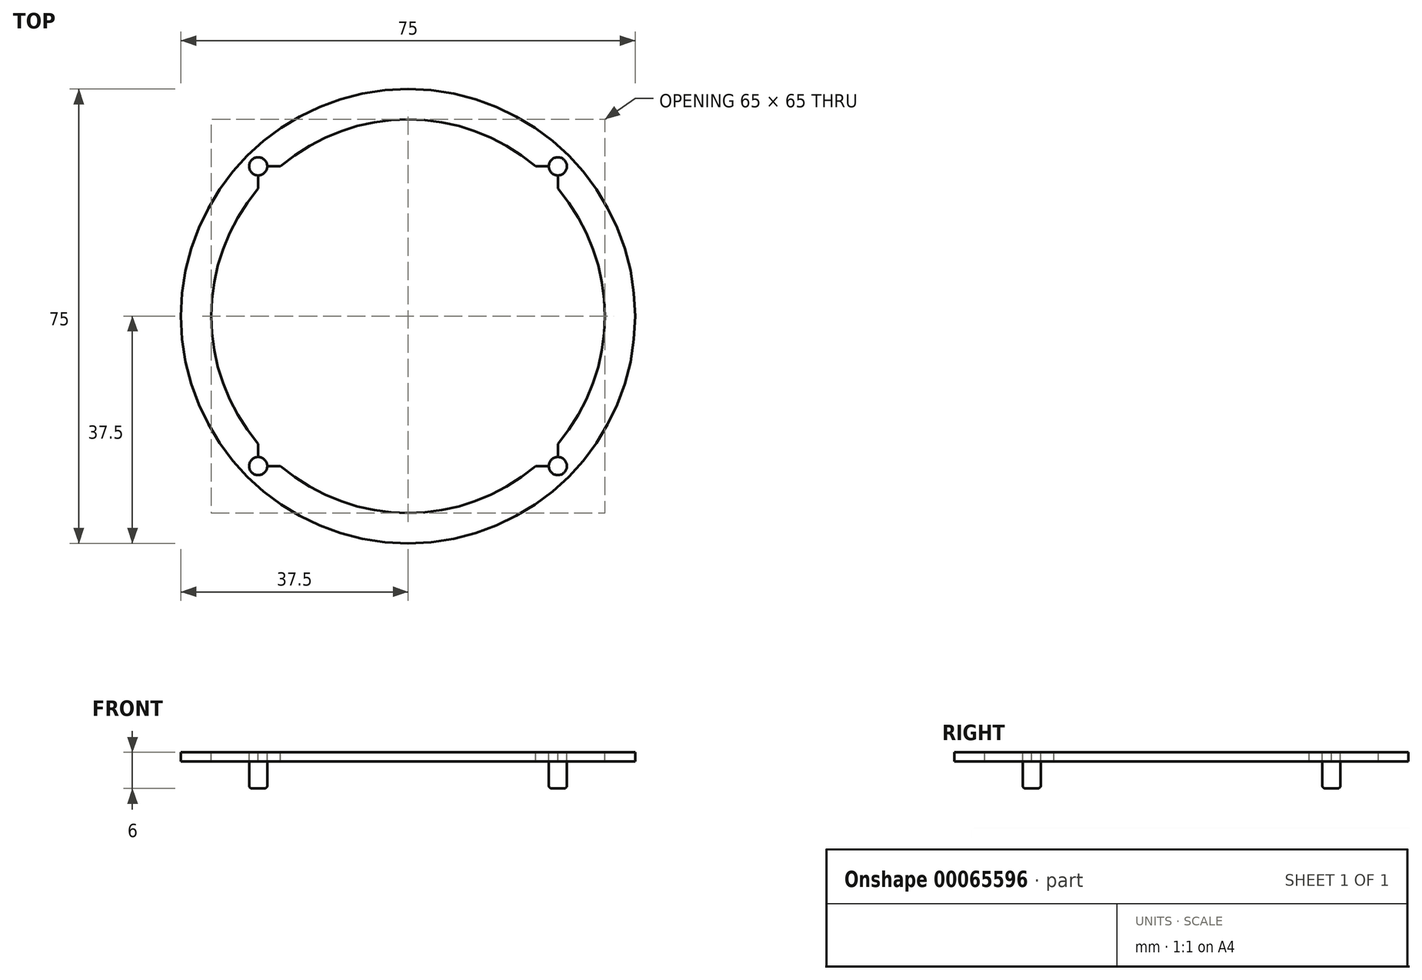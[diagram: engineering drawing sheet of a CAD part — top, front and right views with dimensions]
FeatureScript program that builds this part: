
annotation { "Feature Type Name" : "Feature", "Feature Type Description" : "" }
export const myFeature = defineFeature(function(context is Context, id is Id, definition is map)
    precondition{}
    {
        {
            var Q0;
            Q0=qCreatedBy(makeId("Top.planeOp"),FACE);
            cPlane(context, id + "F0", {"entities" : qUnion([Q0]), "cplaneType" : CPlaneType.OFFSET, "offset" : 1 * mm, "oppositeDirection" : true, "width" : 150 * mm, "height" : 150 * mm});
        }
        {
            var Q0;
            Q0=qCreatedBy(id+"F0.planeOp",FACE);
            var sketch = newSketch(context, id + "F1", { "sketchPlane" : qUnion([Q0])});
            skCircle(sketch, "E0", {"center": v(0, 0) * mm, "radius": 37.5 * mm});
            skCircle(sketch, "E1", {"center": v(0, 0) * mm, "radius": 32.5 * mm});
            skLineSegment(sketch, "E2", {"start": v(0, 0) * mm, "end": v(58.14, 58.14) * mm, "construction": true});
            skLineSegment(sketch, "E3", {"start": v(0, 0) * mm, "end": v(-49.5, 49.5) * mm, "construction": true});
            skLineSegment(sketch, "E4", {"start": v(0, 0) * mm, "end": v(-40.21, -40.21) * mm, "construction": true});
            skLineSegment(sketch, "E5", {"start": v(0, 0) * mm, "end": v(49.5, -49.5) * mm, "construction": true});
            skLineSegment(sketch, "E6", {"start": v(-24.75, 24.75) * mm, "end": v(24.75, 24.75) * mm});
            skLineSegment(sketch, "E7", {"start": v(24.75, 24.75) * mm, "end": v(24.75, -24.75) * mm});
            skLineSegment(sketch, "E8", {"start": v(24.75, -24.75) * mm, "end": v(-24.75, -24.75) * mm});
            skLineSegment(sketch, "E9", {"start": v(-24.75, -24.75) * mm, "end": v(-24.75, 24.75) * mm});
            skCircle(sketch, "E10", {"center": v(-24.75, 24.75) * mm, "radius": 1.5 * mm});
            skCircle(sketch, "E11", {"center": v(24.75, 24.75) * mm, "radius": 1.5 * mm});
            skCircle(sketch, "E12", {"center": v(24.75, -24.75) * mm, "radius": 1.5 * mm});
            skCircle(sketch, "E13", {"center": v(-24.75, -24.75) * mm, "radius": 1.5 * mm});
            skSolve(sketch);
        }
        {
            var Q0;
            {var subQ1=sQuery(id+"F1.wireOp",EDGE,"E9");var subQ3=sQuery(id+"F1.wireOp",EDGE,"E6");var subQ5=makeQuery(id+"F1.imprint","INTERSECT",VERTEX,{"derivedFrom":[subQ3,subQ1]});Q0=makeQuery(id+"F1.imprint","IMPRINT",FACE,{"disambiguationData":[TD([[makeQuery(id+"F1.imprint","IMPRINT",EDGE,{"disambiguationData":[TD([[subQ5,-1.0]])],"derivedFrom":subQ3}),1.0]])]});}
            var Q1;
            {var subQ1=sQuery(id+"F1.wireOp",EDGE,"E9");var subQ3=sQuery(id+"F1.wireOp",EDGE,"E6");var subQ5=makeQuery(id+"F1.imprint","INTERSECT",VERTEX,{"derivedFrom":[subQ3,subQ1]});Q1=makeQuery(id+"F1.imprint","IMPRINT",FACE,{"disambiguationData":[TD([[makeQuery(id+"F1.imprint","IMPRINT",EDGE,{"disambiguationData":[TD([[subQ5,-1.0]])],"derivedFrom":subQ3}),-1.0]])]});}
            var Q2;
            {var subQ1=sQuery(id+"F1.wireOp",EDGE,"E7");var subQ3=sQuery(id+"F1.wireOp",EDGE,"E6");var subQ5=makeQuery(id+"F1.imprint","INTERSECT",VERTEX,{"derivedFrom":[subQ3,subQ1]});Q2=makeQuery(id+"F1.imprint","IMPRINT",FACE,{"disambiguationData":[TD([[makeQuery(id+"F1.imprint","IMPRINT",EDGE,{"disambiguationData":[TD([[subQ5,1.0]])],"derivedFrom":subQ3}),-1.0]])]});}
            var Q3;
            {var subQ0=sQuery(id+"F1.wireOp",EDGE,"E7");var subQ3=sQuery(id+"F1.wireOp",EDGE,"E6");var subQ4=makeQuery(id+"F1.imprint","INTERSECT",VERTEX,{"derivedFrom":[subQ3,subQ0]});Q3=makeQuery(id+"F1.imprint","IMPRINT",FACE,{"disambiguationData":[TD([[makeQuery(id+"F1.imprint","IMPRINT",EDGE,{"disambiguationData":[TD([[subQ4,1.0]])],"derivedFrom":subQ3}),1.0]])]});}
            var Q4;
            {var subQ1=sQuery(id+"F1.wireOp",EDGE,"E8");var subQ3=sQuery(id+"F1.wireOp",EDGE,"E7");var subQ5=makeQuery(id+"F1.imprint","INTERSECT",VERTEX,{"derivedFrom":[subQ3,subQ1]});Q4=makeQuery(id+"F1.imprint","IMPRINT",FACE,{"disambiguationData":[TD([[makeQuery(id+"F1.imprint","IMPRINT",EDGE,{"disambiguationData":[TD([[subQ5,1.0]])],"derivedFrom":subQ3}),1.0]])]});}
            var Q5;
            {var subQ1=sQuery(id+"F1.wireOp",EDGE,"E8");var subQ3=sQuery(id+"F1.wireOp",EDGE,"E7");var subQ5=makeQuery(id+"F1.imprint","INTERSECT",VERTEX,{"derivedFrom":[subQ3,subQ1]});Q5=makeQuery(id+"F1.imprint","IMPRINT",FACE,{"disambiguationData":[TD([[makeQuery(id+"F1.imprint","IMPRINT",EDGE,{"disambiguationData":[TD([[subQ5,1.0]])],"derivedFrom":subQ3}),-1.0]])]});}
            var Q6;
            {var subQ1=sQuery(id+"F1.wireOp",EDGE,"E9");var subQ3=sQuery(id+"F1.wireOp",EDGE,"E8");var subQ5=makeQuery(id+"F1.imprint","INTERSECT",VERTEX,{"derivedFrom":[subQ3,subQ1]});Q6=makeQuery(id+"F1.imprint","IMPRINT",FACE,{"disambiguationData":[TD([[makeQuery(id+"F1.imprint","IMPRINT",EDGE,{"disambiguationData":[TD([[subQ5,1.0]])],"derivedFrom":subQ3}),-1.0]])]});}
            var Q7;
            {var subQ0=sQuery(id+"F1.wireOp",EDGE,"E9");var subQ3=sQuery(id+"F1.wireOp",EDGE,"E8");var subQ4=makeQuery(id+"F1.imprint","INTERSECT",VERTEX,{"derivedFrom":[subQ3,subQ0]});Q7=makeQuery(id+"F1.imprint","IMPRINT",FACE,{"disambiguationData":[TD([[makeQuery(id+"F1.imprint","IMPRINT",EDGE,{"disambiguationData":[TD([[subQ4,1.0]])],"derivedFrom":subQ3}),1.0]])]});}
            extrude(context, id + "F2", {"entities" : qUnion([Q0, Q1, Q2, Q3, Q4, Q5, Q6, Q7]), "oppositeDirection" : true, "depth" : 6 * mm});
        }
        {
            var Q0;
            {var subQ0=sQuery(id+"F1.wireOp",EDGE,"E1");var subQ1=sQuery(id+"F1.wireOp",EDGE,"E6");Q0=makeQuery(id+"F8vz59gYwAsgNgq_0.opExtrude","CAP_EDGE",EDGE,{"disambiguationData":[OSD([subQ0]),TDD([makeQuery(id+"F1.imprint","IMPRINT",EDGE,{"disambiguationData":[TD([[makeQuery(id+"F1.imprint","INTERSECT",VERTEX,{"disambiguationData":[OD(0.0)],"derivedFrom":[subQ0,subQ1]}),-1.0]])],"derivedFrom":subQ0})])],"isStart":true});}
            var Q1;
            {var subQ0=sQuery(id+"F1.wireOp",EDGE,"E1");var subQ1=sQuery(id+"F1.wireOp",EDGE,"E9");Q1=makeQuery(id+"F8vz59gYwAsgNgq_0.opExtrude","CAP_EDGE",EDGE,{"disambiguationData":[OSD([subQ0]),TDD([makeQuery(id+"F1.imprint","IMPRINT",EDGE,{"disambiguationData":[TD([[makeQuery(id+"F1.imprint","INTERSECT",VERTEX,{"disambiguationData":[OD(0.0)],"derivedFrom":[subQ0,subQ1]}),-1.0]])],"derivedFrom":subQ0})])],"isStart":true});}
            var Q2;
            {var subQ0=sQuery(id+"F1.wireOp",EDGE,"E1");var subQ1=sQuery(id+"F1.wireOp",EDGE,"E8");Q2=makeQuery(id+"F8vz59gYwAsgNgq_0.opExtrude","CAP_EDGE",EDGE,{"disambiguationData":[OSD([subQ0]),TDD([makeQuery(id+"F1.imprint","IMPRINT",EDGE,{"disambiguationData":[TD([[makeQuery(id+"F1.imprint","INTERSECT",VERTEX,{"disambiguationData":[OD(0.0)],"derivedFrom":[subQ0,subQ1]}),-1.0]])],"derivedFrom":subQ0})])],"isStart":true});}
            var Q3;
            {var subQ0=sQuery(id+"F1.wireOp",EDGE,"E1");var subQ1=sQuery(id+"F1.wireOp",EDGE,"E7");Q3=makeQuery(id+"F8vz59gYwAsgNgq_0.opExtrude","CAP_EDGE",EDGE,{"disambiguationData":[OSD([subQ0]),TDD([makeQuery(id+"F1.imprint","IMPRINT",EDGE,{"disambiguationData":[TD([[makeQuery(id+"F1.imprint","INTERSECT",VERTEX,{"disambiguationData":[OD(0.0)],"derivedFrom":[subQ0,subQ1]}),1.0]])],"derivedFrom":subQ0})])],"isStart":true});}
            var Q4;
            Q4=makeQuery(id+"F2.opExtrude","CAP_EDGE",EDGE,{"disambiguationData":[OSD([sQuery(id+"F1.wireOp",EDGE,"E11")])],"isStart":false});
            var Q5;
            Q5=makeQuery(id+"F2.opExtrude","CAP_EDGE",EDGE,{"disambiguationData":[OSD([sQuery(id+"F1.wireOp",EDGE,"E12")])],"isStart":false});
            var Q6;
            Q6=makeQuery(id+"F2.opExtrude","CAP_EDGE",EDGE,{"disambiguationData":[OSD([sQuery(id+"F1.wireOp",EDGE,"E10")])],"isStart":false});
            var Q7;
            Q7=makeQuery(id+"F2.opExtrude","CAP_EDGE",EDGE,{"disambiguationData":[OSD([sQuery(id+"F1.wireOp",EDGE,"E13")])],"isStart":false});
            fillet(context, id + "F3", {"entities" : qUnion([Q0, Q1, Q2, Q3, Q4, Q5, Q6, Q7]), "radius" : .5 * mm, "tangentPropagation" : true, "allowEdgeOverflow" : false});
        }
        {
            var Q0;
            Q0=makeQuery(id+"F1.imprint","IMPRINT",FACE,{"disambiguationData":[TD([[makeQuery(id+"F1.imprint","IMPRINT",EDGE,{"derivedFrom":sQuery(id+"F1.wireOp",EDGE,"E0")}),1.0]])]});
            var Q1;
            {var subQ1=sQuery(id+"F1.wireOp",EDGE,"E9");var subQ5=sQuery(id+"F1.wireOp",EDGE,"E1");var subQ6=makeQuery(id+"F1.imprint","INTERSECT",VERTEX,{"disambiguationData":[OD(1.0)],"derivedFrom":[subQ5,subQ1]});Q1=makeQuery(id+"F1.imprint","IMPRINT",FACE,{"disambiguationData":[TD([[makeQuery(id+"F1.imprint","IMPRINT",EDGE,{"disambiguationData":[TD([[subQ6,-1.0]])],"derivedFrom":subQ5}),-1.0]])]});}
            var Q2;
            {var subQ3=sQuery(id+"F1.wireOp",EDGE,"E6");var subQ5=sQuery(id+"F1.wireOp",EDGE,"E1");var subQ6=makeQuery(id+"F1.imprint","INTERSECT",VERTEX,{"disambiguationData":[OD(1.0)],"derivedFrom":[subQ5,subQ3]});Q2=makeQuery(id+"F1.imprint","IMPRINT",FACE,{"disambiguationData":[TD([[makeQuery(id+"F1.imprint","IMPRINT",EDGE,{"disambiguationData":[TD([[subQ6,-1.0]])],"derivedFrom":subQ5}),-1.0]])]});}
            var Q3;
            {var subQ3=sQuery(id+"F1.wireOp",EDGE,"E6");var subQ5=sQuery(id+"F1.wireOp",EDGE,"E1");var subQ7=makeQuery(id+"F1.imprint","INTERSECT",VERTEX,{"disambiguationData":[OD(0.0)],"derivedFrom":[subQ5,subQ3]});Q3=makeQuery(id+"F1.imprint","IMPRINT",FACE,{"disambiguationData":[TD([[makeQuery(id+"F1.imprint","IMPRINT",EDGE,{"disambiguationData":[TD([[subQ7,1.0]])],"derivedFrom":subQ5}),-1.0]])]});}
            var Q4;
            {var subQ1=sQuery(id+"F1.wireOp",EDGE,"E8");var subQ5=sQuery(id+"F1.wireOp",EDGE,"E1");var subQ6=makeQuery(id+"F1.imprint","INTERSECT",VERTEX,{"disambiguationData":[OD(1.0)],"derivedFrom":[subQ5,subQ1]});Q4=makeQuery(id+"F1.imprint","IMPRINT",FACE,{"disambiguationData":[TD([[makeQuery(id+"F1.imprint","IMPRINT",EDGE,{"disambiguationData":[TD([[subQ6,-1.0]])],"derivedFrom":subQ5}),-1.0]])]});}
            extrude(context, id + "F4", {"entities" : qUnion([Q0, Q1, Q2, Q3, Q4]), "oppositeDirection" : true, "depth" : 1.5 * mm});
        }
    });
